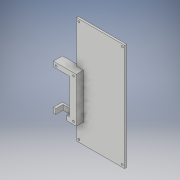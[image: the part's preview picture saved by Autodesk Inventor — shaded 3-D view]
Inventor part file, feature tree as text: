
AUTODESK INVENTOR PART (.ipt)
format: ipt  version: 2019 (Build 230136000, 136)  size: 162,304 bytes
history: native  units: in
note: dims shown in document units (in); Inventor stores cm internally (conversion verified against a paired STEP export)
features: sketch x4, extrude x2, hole x2
ambient origin geometry x8: Origin, YZ Plane, XZ Plane, XY Plane, X Axis, Y Axis, Z Axis, Center Point
bodies: Solid1 (feature_tree)
feature tree (8):
  extrude  "Extrusion1"  Depth=2.13in
  hole  "Hole1"  [1 undecoded]
  extrude  "Extrusion2"  Depth=0.12in
  hole  "Hole2"  [1 undecoded]
  sketch  "Sketch1"  dims[d0=2.43in d1=2.13in]
  sketch  "Sketch2"  dims[d4=1.0in d5=0.1in d6=0.0in]
  sketch  "Sketch3"  dims[d7=0.12in d8=0.12in]
  sketch  "Sketch4"  dims[d9=0.12in d10=0.12in d11=0.1in d12=0.75in d13=0.375in d14=0.25in d15=0.5635in d16=1.0in d17=0.8108in d22=0.81in d23=0.25in d24=0.25in d25=0.125in d26=0.125in d27=0.36in d28=0.0in d29=0.14in d30=0.14in d31=0.14in d32=0.14in d33=0.35in d34=0.1in d35=0.75in d36=0.375in d37=0.25in d38=0.5635in d39=0.18in d40=0.8108in d41=0.14in]
note: 2 required parameter values undecoded (feature->parameter linkage not recoverable at this tier; creation-order binding heuristic only, values carry confidence <= 0.55)
